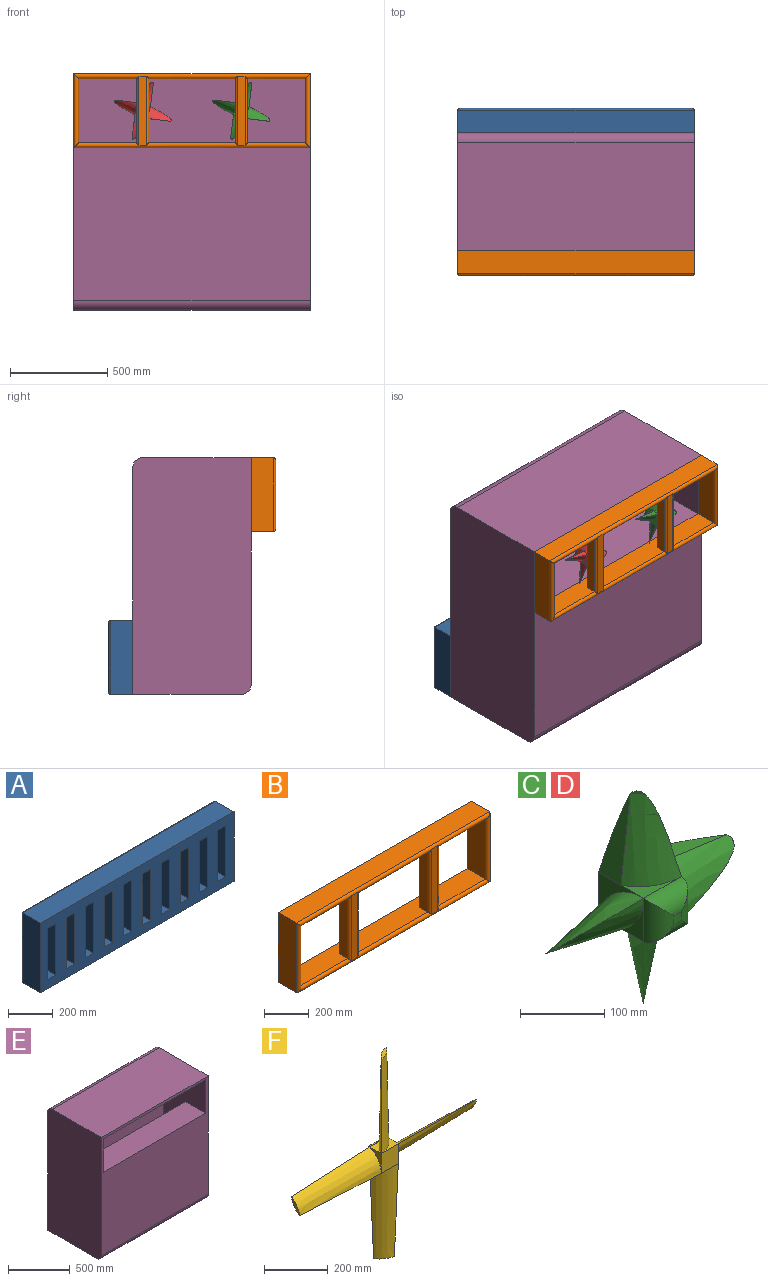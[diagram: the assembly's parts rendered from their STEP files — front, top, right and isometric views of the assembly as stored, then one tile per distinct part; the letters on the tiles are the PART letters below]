
ASSEMBLY  parts=6 mates=5
PART A: 90 faces, bbox 1219.2x127x381 mm
  f0: plane 1193.8x355.6mm, normal (0,1,0), area 192257.7mm2, adj f46,f47,f48,f49,f50,f51,f52,f53
  f1: plane 1219.2x381mm, normal (0,-1,0), area 322580mm2, adj f2,f3,f4,f5,f6,f7,f8,f9
  f2: plane 1219.2x114.3mm, normal (0,0,1), area 139354.6mm2, adj f1,f3,f5,f86
  f3: plane 381x114.3mm, normal (1,0,0), area 43548.3mm2, adj f1,f2,f4,f87
  f4: plane 1219.2x114.3mm, normal (0,0,-1), area 139354.6mm2, adj f1,f3,f5,f89
  f5: plane 381x114.3mm, normal (-1,0,0), area 43548.3mm2, adj f1,f2,f4,f88
  f6: plane 279.4x114.3mm, normal (1,0,0), area 31935.4mm2, adj f1,f7,f9,f84
  f7: plane 114.3x50.8mm, normal (0,0,-1), area 5806.4mm2, adj f1,f6,f8,f85
  f8: plane 279.4x114.3mm, normal (-1,0,0), area 31935.4mm2, adj f1,f7,f9,f83
  f9: plane 114.3x50.8mm, normal (0,0,1), area 5806.4mm2, adj f1,f6,f8,f82
  f10: plane 279.4x114.3mm, normal (1,0,0), area 31935.4mm2, adj f1,f11,f13,f78
  f11: plane 114.3x50.8mm, normal (0,0,-1), area 5806.4mm2, adj f1,f10,f12,f79
  f12: plane 279.4x114.3mm, normal (-1,0,0), area 31935.4mm2, adj f1,f11,f13,f81
  f13: plane 114.3x50.8mm, normal (0,0,1), area 5806.4mm2, adj f1,f10,f12,f80
  f14: plane 279.4x114.3mm, normal (1,0,0), area 31935.4mm2, adj f1,f15,f17,f76
  f15: plane 114.3x50.8mm, normal (0,0,-1), area 5806.4mm2, adj f1,f14,f16,f77
  f16: plane 279.4x114.3mm, normal (-1,0,0), area 31935.4mm2, adj f1,f15,f17,f75
  f17: plane 114.3x50.8mm, normal (0,0,1), area 5806.4mm2, adj f1,f14,f16,f74
  f18: plane 279.4x114.3mm, normal (1,0,0), area 31935.4mm2, adj f1,f19,f21,f72
  f19: plane 114.3x50.8mm, normal (0,0,-1), area 5806.4mm2, adj f1,f18,f20,f73
  f20: plane 279.4x114.3mm, normal (-1,0,0), area 31935.4mm2, adj f1,f19,f21,f71
  f21: plane 114.3x50.8mm, normal (0,0,1), area 5806.4mm2, adj f1,f18,f20,f70
  f22: plane 279.4x114.3mm, normal (1,0,0), area 31935.4mm2, adj f1,f23,f25,f68
  f23: plane 114.3x50.8mm, normal (0,0,-1), area 5806.4mm2, adj f1,f22,f24,f69
  f24: plane 279.4x114.3mm, normal (-1,0,0), area 31935.4mm2, adj f1,f23,f25,f67
  f25: plane 114.3x50.8mm, normal (0,0,1), area 5806.4mm2, adj f1,f22,f24,f66
  f26: plane 279.4x114.3mm, normal (1,0,0), area 31935.4mm2, adj f1,f27,f29,f64
  f27: plane 114.3x50.8mm, normal (0,0,-1), area 5806.4mm2, adj f1,f26,f28,f65
  f28: plane 279.4x114.3mm, normal (-1,0,0), area 31935.4mm2, adj f1,f27,f29,f63
  f29: plane 114.3x50.8mm, normal (0,0,1), area 5806.4mm2, adj f1,f26,f28,f62
  f30: plane 279.4x114.3mm, normal (1,0,0), area 31935.4mm2, adj f1,f31,f33,f60
  f31: plane 114.3x50.8mm, normal (0,0,-1), area 5806.4mm2, adj f1,f30,f32,f61
  f32: plane 279.4x114.3mm, normal (-1,0,0), area 31935.4mm2, adj f1,f31,f33,f59
  f33: plane 114.3x50.8mm, normal (0,0,1), area 5806.4mm2, adj f1,f30,f32,f58
  f34: plane 279.4x114.3mm, normal (1,0,0), area 31935.4mm2, adj f1,f35,f37,f56
  f35: plane 114.3x50.8mm, normal (0,0,-1), area 5806.4mm2, adj f1,f34,f36,f57
  f36: plane 279.4x114.3mm, normal (-1,0,0), area 31935.4mm2, adj f1,f35,f37,f55
  f37: plane 114.3x50.8mm, normal (0,0,1), area 5806.4mm2, adj f1,f34,f36,f54
  f38: plane 279.4x114.3mm, normal (1,0,0), area 31935.4mm2, adj f1,f39,f41,f52
  f39: plane 114.3x50.8mm, normal (0,0,-1), area 5806.4mm2, adj f1,f38,f40,f53
  f40: plane 279.4x114.3mm, normal (-1,0,0), area 31935.4mm2, adj f1,f39,f41,f51
  f41: plane 114.3x50.8mm, normal (0,0,1), area 5806.4mm2, adj f1,f38,f40,f50
  f42: plane 279.4x114.3mm, normal (1,0,0), area 31935.4mm2, adj f1,f43,f45,f48
  f43: plane 114.3x50.8mm, normal (0,0,-1), area 5806.4mm2, adj f1,f42,f44,f49
  f44: plane 279.4x114.3mm, normal (-1,0,0), area 31935.4mm2, adj f1,f43,f45,f47
  f45: plane 114.3x50.8mm, normal (0,0,1), area 5806.4mm2, adj f1,f42,f44,f46
  f46: cylinder r=12.7mm len=76.2mm, axis (1,0,0), area 1197.5mm2, adj f0,f45,f47,f48
  f47: cylinder r=12.7mm len=304.8mm, axis (0,0,1), area 5757.9mm2, adj f0,f44,f46,f49
  f48: cylinder r=12.7mm len=304.8mm, axis (0,0,-1), area 5757.9mm2, adj f0,f42,f46,f49
  f49: cylinder r=12.7mm len=76.2mm, axis (-1,0,0), area 1197.5mm2, adj f0,f43,f47,f48
  f50: cylinder r=12.7mm len=76.2mm, axis (1,0,0), area 1197.5mm2, adj f0,f41,f51,f52
  f51: cylinder r=12.7mm len=304.8mm, axis (0,0,1), area 5757.9mm2, adj f0,f40,f50,f53
  f52: cylinder r=12.7mm len=304.8mm, axis (0,0,-1), area 5757.9mm2, adj f0,f38,f50,f53
  f53: cylinder r=12.7mm len=76.2mm, axis (-1,0,0), area 1197.5mm2, adj f0,f39,f51,f52
  f54: cylinder r=12.7mm len=76.2mm, axis (1,0,0), area 1197.5mm2, adj f0,f37,f55,f56
  f55: cylinder r=12.7mm len=304.8mm, axis (0,0,1), area 5757.9mm2, adj f0,f36,f54,f57
  f56: cylinder r=12.7mm len=304.8mm, axis (0,0,-1), area 5757.9mm2, adj f0,f34,f54,f57
  f57: cylinder r=12.7mm len=76.2mm, axis (-1,0,0), area 1197.5mm2, adj f0,f35,f55,f56
  f58: cylinder r=12.7mm len=76.2mm, axis (1,0,0), area 1197.5mm2, adj f0,f33,f59,f60
  f59: cylinder r=12.7mm len=304.8mm, axis (0,0,1), area 5757.9mm2, adj f0,f32,f58,f61
  f60: cylinder r=12.7mm len=304.8mm, axis (0,0,-1), area 5757.9mm2, adj f0,f30,f58,f61
  f61: cylinder r=12.7mm len=76.2mm, axis (-1,0,0), area 1197.5mm2, adj f0,f31,f59,f60
  f62: cylinder r=12.7mm len=76.2mm, axis (1,0,0), area 1197.5mm2, adj f0,f29,f63,f64
  f63: cylinder r=12.7mm len=304.8mm, axis (0,0,1), area 5757.9mm2, adj f0,f28,f62,f65
  f64: cylinder r=12.7mm len=304.8mm, axis (0,0,-1), area 5757.9mm2, adj f0,f26,f62,f65
  f65: cylinder r=12.7mm len=76.2mm, axis (-1,0,0), area 1197.5mm2, adj f0,f27,f63,f64
  f66: cylinder r=12.7mm len=76.2mm, axis (1,0,0), area 1197.5mm2, adj f0,f25,f67,f68
  f67: cylinder r=12.7mm len=304.8mm, axis (0,0,1), area 5757.9mm2, adj f0,f24,f66,f69
  f68: cylinder r=12.7mm len=304.8mm, axis (0,0,-1), area 5757.9mm2, adj f0,f22,f66,f69
  f69: cylinder r=12.7mm len=76.2mm, axis (-1,0,0), area 1197.5mm2, adj f0,f23,f67,f68
  f70: cylinder r=12.7mm len=76.2mm, axis (1,0,0), area 1197.5mm2, adj f0,f21,f71,f72
  f71: cylinder r=12.7mm len=304.8mm, axis (0,0,1), area 5757.9mm2, adj f0,f20,f70,f73
  f72: cylinder r=12.7mm len=304.8mm, axis (0,0,-1), area 5757.9mm2, adj f0,f18,f70,f73
  f73: cylinder r=12.7mm len=76.2mm, axis (-1,0,0), area 1197.5mm2, adj f0,f19,f71,f72
  f74: cylinder r=12.7mm len=76.2mm, axis (1,0,0), area 1197.5mm2, adj f0,f17,f75,f76
  f75: cylinder r=12.7mm len=304.8mm, axis (0,0,1), area 5757.9mm2, adj f0,f16,f74,f77
  f76: cylinder r=12.7mm len=304.8mm, axis (0,0,-1), area 5757.9mm2, adj f0,f14,f74,f77
  f77: cylinder r=12.7mm len=76.2mm, axis (-1,0,0), area 1197.5mm2, adj f0,f15,f75,f76
  f78: cylinder r=12.7mm len=304.8mm, axis (0,0,-1), area 5757.9mm2, adj f0,f10,f79,f80
  f79: cylinder r=12.7mm len=76.2mm, axis (-1,0,0), area 1197.5mm2, adj f0,f11,f78,f81
  f80: cylinder r=12.7mm len=76.2mm, axis (1,0,0), area 1197.5mm2, adj f0,f13,f78,f81
  f81: cylinder r=12.7mm len=304.8mm, axis (0,0,1), area 5757.9mm2, adj f0,f12,f79,f80
  f82: cylinder r=12.7mm len=76.2mm, axis (1,0,0), area 1197.5mm2, adj f0,f9,f83,f84
  f83: cylinder r=12.7mm len=304.8mm, axis (0,0,1), area 5757.9mm2, adj f0,f8,f82,f85
  f84: cylinder r=12.7mm len=304.8mm, axis (0,0,-1), area 5757.9mm2, adj f0,f6,f82,f85
  f85: cylinder r=12.7mm len=76.2mm, axis (-1,0,0), area 1197.5mm2, adj f0,f7,f83,f84
  f86: cylinder r=12.7mm len=1219.2mm, axis (-1,0,0), area 24137.8mm2, adj f0,f2,f87,f88
  f87: cylinder r=12.7mm len=381mm, axis (0,0,1), area 7416.5mm2, adj f0,f3,f86,f89
  f88: cylinder r=12.7mm len=381mm, axis (0,0,-1), area 7416.5mm2, adj f0,f5,f86,f89
  f89: cylinder r=12.7mm len=1219.2mm, axis (1,0,0), area 24137.8mm2, adj f0,f4,f87,f88
PART B: 25 faces, bbox 1219.2x127x381 mm
  f0: plane 355.6x38.1mm, normal (0,-1,0), area 13548.4mm2, adj f17,f19,f20,f22
  f1: plane 355.6x38.1mm, normal (0,-1,0), area 13548.4mm2, adj f17,f18,f22,f24
  f2: plane 1219.2x381mm, normal (0,1,0), area 78709.5mm2, adj f3,f4,f5,f6,f7,f8,f9,f10
  f3: plane 381x114.3mm, normal (-1,0,0), area 43548.3mm2, adj f2,f4,f6,f21
  f4: plane 1219.2x114.3mm, normal (0,0,-1), area 139354.6mm2, adj f2,f3,f5,f17
  f5: plane 381x114.3mm, normal (1,0,0), area 43548.3mm2, adj f2,f4,f6,f23
  f6: plane 1219.2x114.3mm, normal (0,0,1), area 139354.6mm2, adj f2,f3,f5,f22
  f7: plane 1168.4x114.3mm, normal (0,0,-1), area 127096.5mm2, adj f2,f8,f10,f11,f12,f13,f14,f15
  f8: plane 330.2x114.3mm, normal (1,0,0), area 37741.9mm2, adj f2,f7,f9,f21
  f9: plane 1168.4x114.3mm, normal (0,0,1), area 127096.5mm2, adj f2,f8,f10,f11,f12,f13,f14,f15
  f10: plane 330.2x114.3mm, normal (-1,0,0), area 37741.9mm2, adj f2,f7,f9,f23
  f11: plane 330.2x50.8mm, normal (1,0,0), area 16774.2mm2, adj f7,f9,f13,f19
  f12: plane 330.2x50.8mm, normal (-1,0,0), area 16774.2mm2, adj f7,f9,f13,f20
  f13: plane 330.2x63.5mm, normal (0,1,0), area 20967.7mm2, adj f7,f9,f11,f12
  f14: plane 330.2x50.8mm, normal (1,0,0), area 16774.2mm2, adj f7,f9,f16,f24
  f15: plane 330.2x50.8mm, normal (-1,0,0), area 16774.2mm2, adj f7,f9,f16,f18
  f16: plane 330.2x63.5mm, normal (0,1,0), area 20967.7mm2, adj f7,f9,f14,f15
  f17: cylinder r=12.7mm len=1219.2mm, axis (-1,0,0), area 45465.2mm2, adj f0,f1,f4,f9,f18,f19,f20,f21
  f18: cylinder r=12.7mm len=355.6mm, axis (0,0,-1), area 6771.3mm2, adj f1,f15,f17,f22
  f19: cylinder r=12.7mm len=355.6mm, axis (0,0,1), area 6771.3mm2, adj f0,f11,f17,f22
  f20: cylinder r=12.7mm len=355.6mm, axis (0,0,-1), area 6771.3mm2, adj f0,f12,f17,f22
  f21: cylinder r=12.7mm len=381mm, axis (0,0,1), area 14187.8mm2, adj f3,f8,f17,f22
  f22: cylinder r=12.7mm len=1219.2mm, axis (1,0,0), area 45465.2mm2, adj f0,f1,f6,f7,f18,f19,f20,f21
  f23: cylinder r=12.7mm len=381mm, axis (0,0,-1), area 14187.8mm2, adj f5,f10,f17,f22
  f24: cylinder r=12.7mm len=355.6mm, axis (0,0,1), area 6771.3mm2, adj f1,f14,f17,f22
PART C: 26 faces, bbox 311.3x101.6x311.3 mm
  f0: plane 76.2x63.5mm, normal (0,0,1), area 1201.4mm2, adj f4,f8,f9,f21
  f1: plane 76.2x63.5mm, normal (-1,0,0), area 1201.4mm2, adj f5,f8,f17,f19
  f2: plane 76.2x63.5mm, normal (0,0,-1), area 1201.4mm2, adj f6,f8,f14,f18
  f3: plane 76.2x63.5mm, normal (1,0,0), area 1201.4mm2, adj f7,f8,f11,f15
  f4: plane 63.5x38.1mm, normal (1,0,0), area 695.7mm2, adj f0,f10,f24
  f5: plane 63.5x38.1mm, normal (0,0,1), area 695.7mm2, adj f1,f20,f22
  f6: plane 63.5x38.1mm, normal (-1,0,0), area 695.7mm2, adj f2,f16,f23
  f7: plane 63.5x38.1mm, normal (0,0,-1), area 695.7mm2, adj f3,f13,f25
  f8: plane 63.5x63.5mm, normal (0,1,0), area 4032.2mm2, adj f0,f1,f2,f3
  f9: plane 120.31x38.1mm, normal (0.17,0,0.98), area 2515mm2, adj f0,f10,f11
  f10: cone r=71.97mm half-angle=10deg, axis (-1,0,0), area 6254.7mm2, adj f4,f9,f11
  f11: cone r=77.47mm half-angle=10deg, axis (-1,0,0), area 8170.4mm2, adj f3,f9,f10
  f12: plane 12.7x12.7mm, normal (0,-1,0), area 161.3mm2, adj f22,f23,f24,f25
  f13: cone r=71.97mm half-angle=10deg, axis (0,0,1), area 6254.7mm2, adj f7,f14,f15
  f14: cone r=77.47mm half-angle=10deg, axis (0,0,1), area 8170.4mm2, adj f2,f13,f15
  f15: plane 120.31x38.1mm, normal (0.98,0,-0.17), area 2515mm2, adj f3,f13,f14
  f16: cone r=71.97mm half-angle=10deg, axis (1,0,0), area 6254.7mm2, adj f6,f17,f18
  f17: cone r=77.47mm half-angle=10deg, axis (1,0,0), area 8170.4mm2, adj f1,f16,f18
  f18: plane 120.31x38.1mm, normal (-0.17,0,-0.98), area 2515mm2, adj f2,f16,f17
  f19: plane 120.31x38.1mm, normal (-0.98,0,0.17), area 2515mm2, adj f1,f20,f21
  f20: cone r=71.97mm half-angle=10deg, axis (0,0,-1), area 6254.7mm2, adj f5,f19,f21
  f21: cone r=77.47mm half-angle=10deg, axis (0,0,-1), area 8170.4mm2, adj f0,f19,f20
  f22: cylinder r=25.4mm len=63.5mm, axis (1,0,0), area 1797mm2, adj f5,f12,f23,f24
  f23: cylinder r=25.4mm len=63.5mm, axis (0,0,1), area 1797mm2, adj f6,f12,f22,f25
  f24: cylinder r=25.4mm len=63.5mm, axis (0,0,-1), area 1797mm2, adj f4,f12,f22,f25
  f25: cylinder r=25.4mm len=63.5mm, axis (1,0,0), area 1797mm2, adj f7,f12,f23,f24
PART D: same geometry as C
PART E: 18 faces, bbox 1219.2x609.6x1219.2 mm
  f0: plane 1168.4x228.6mm, normal (0,0,1), area 267096.2mm2, adj f5,f11,f12,f15
  f1: plane 279.4x127mm, normal (1,0,0), area 35483.8mm2, adj f2,f4,f13,f14
  f2: plane 1125.22x127mm, normal (0,0,-1), area 142902.9mm2, adj f1,f3,f4,f13
  f3: plane 279.4x127mm, normal (-1,0,0), area 35483.8mm2, adj f2,f4,f13,f14
  f4: plane 1219.2x1168.4mm, normal (0,1,0), area 1110126.8mm2, adj f1,f2,f3,f6,f7,f9,f14,f17
  f5: plane 1219.2x1168.4mm, normal (0,-1,0), area 1038707.6mm2, adj f0,f6,f7,f8,f10,f11,f12,f16
  f6: plane 1219.2x609.6mm, normal (1,0,0), area 742116.7mm2, adj f4,f5,f8,f9,f16,f17
  f7: plane 1219.2x609.6mm, normal (-1,0,0), area 742116.7mm2, adj f4,f5,f8,f9,f16,f17
  f8: plane 1219.2x558.8mm, normal (0,0,1), area 681289mm2, adj f5,f6,f7,f17
  f9: plane 1219.2x558.8mm, normal (0,0,-1), area 681289mm2, adj f4,f6,f7,f16
  f10: plane 1168.4x482.6mm, normal (0,0,-1), area 563869.8mm2, adj f5,f11,f12,f13
  f11: plane 1143x482.6mm, normal (1,0,0), area 365805.7mm2, adj f0,f5,f10,f13,f14,f15
  f12: plane 1143x482.6mm, normal (-1,0,0), area 365805.7mm2, adj f0,f5,f10,f13,f14,f15
  f13: plane 1168.4x1143mm, normal (0,-1,0), area 1021094.7mm2, adj f1,f2,f3,f10,f11,f12,f14
  f14: plane 1168.4x381mm, normal (0,0,1), area 439676.5mm2, adj f1,f3,f4,f11,f12,f13,f15
  f15: plane 1168.4x812.8mm, normal (0,1,0), area 949675.5mm2, adj f0,f11,f12,f14
  f16: cylinder r=50.8mm len=1219.2mm, axis (1,0,0), area 97287.8mm2, adj f5,f6,f7,f9
  f17: cylinder r=50.8mm len=1219.2mm, axis (1,0,0), area 97287.8mm2, adj f4,f6,f7,f8
PART F: 43 faces, bbox 787.4x65.9x787.4 mm
  f0: plane 0.04x0mm, normal (-1,0,0), area 0mm2, adj f5,f6,f11
  f1: plane 50.7x0.04mm, normal (-1,0,0), area 2.2mm2, adj f5,f7,f10,f12
  f2: plane 50.8x0.04mm, normal (1,0,0), area 2.2mm2, adj f4,f5,f7,f14
  f3: cone r=82.55mm half-angle=1deg, axis (-1,0,0), area 29676.2mm2, adj f4,f6,f8,f13,f18
  f4: cone r=82.55mm half-angle=1deg, axis (-1,0,0), area 29676.2mm2, adj f2,f3,f8,f14,f18
  f5: plane 76.2x50.8mm, normal (0,0,-1), area 2147.5mm2, adj f0,f1,f2,f6,f7,f11,f12
  f6: plane 76.29x76.29mm, normal (0,1,0), area 19.5mm2, adj f0,f3,f5,f11,f13,f16,f18,f20
  f7: plane 76.29x76.29mm, normal (0,-1,0), area 5819.5mm2, adj f1,f2,f5,f10,f14,f15,f18,f21
  f8: plane 55.46x36.97mm, normal (1,0,0), area 687.6mm2, adj f3,f4
  f9: plane 50.8x50.8mm, normal (0,1,0), area 2574.1mm2, adj f31,f32,f33,f34,f35,f36,f37,f38
  f10: plane 50.8x0.04mm, normal (0,0,-1), area 2.2mm2, adj f1,f7,f12,f29
  f11: cone r=82.55mm half-angle=1deg, axis (0,0,1), area 29676.2mm2, adj f0,f5,f6,f12,f30
  f12: cone r=82.55mm half-angle=1deg, axis (0,0,1), area 29676.2mm2, adj f1,f5,f10,f11,f30
  f13: plane 0.04x0mm, normal (0,0,-1), area 0mm2, adj f3,f6,f18
  f14: plane 50.7x0.04mm, normal (0,0,-1), area 2.2mm2, adj f2,f4,f7,f18
  f15: plane 50.8x0.04mm, normal (0,0,1), area 2.2mm2, adj f7,f17,f18,f24
  f16: cone r=82.55mm half-angle=1deg, axis (0,0,-1), area 29676.2mm2, adj f6,f17,f19,f20,f25
  f17: cone r=82.55mm half-angle=1deg, axis (0,0,-1), area 29676.2mm2, adj f15,f16,f19,f24,f25
  f18: plane 76.2x50.8mm, normal (1,0,0), area 2147.5mm2, adj f3,f4,f6,f7,f13,f14,f15
  f19: plane 55.46x36.97mm, normal (0,0,1), area 687.6mm2, adj f16,f17
  f20: plane 0.04x0mm, normal (1,0,0), area 0mm2, adj f6,f16,f25
  f21: plane 50.8x0.04mm, normal (-1,0,0), area 2.2mm2, adj f7,f23,f25,f28
  f22: cone r=82.55mm half-angle=1deg, axis (1,0,0), area 29676.2mm2, adj f6,f23,f26,f27,f29
  f23: cone r=82.55mm half-angle=1deg, axis (1,0,0), area 29676.2mm2, adj f21,f22,f26,f28,f29
  f24: plane 50.7x0.04mm, normal (1,0,0), area 2.2mm2, adj f7,f15,f17,f25
  f25: plane 76.2x50.8mm, normal (0,0,1), area 2147.5mm2, adj f6,f7,f16,f17,f20,f21,f24
  f26: plane 55.46x36.97mm, normal (-1,0,0), area 687.6mm2, adj f22,f23
  f27: plane 0.04x0mm, normal (0,0,1), area 0mm2, adj f6,f22,f29
  f28: plane 50.7x0.04mm, normal (0,0,1), area 2.2mm2, adj f7,f21,f23,f29
  f29: plane 76.2x50.8mm, normal (-1,0,0), area 2147.5mm2, adj f6,f7,f10,f22,f23,f27,f28
  f30: plane 55.46x36.97mm, normal (0,0,-1), area 687.6mm2, adj f11,f12
  f31: cylinder r=12.7mm len=50.8mm, axis (0,0,-1), area 760.1mm2, adj f6,f9,f32,f33
  f32: cylinder r=12.7mm len=38.06mm, axis (-1,0,0), area 575.1mm2, adj f6,f9,f31,f34
  f33: cylinder r=12.7mm len=12.74mm, axis (-1,0,0), area 0.9mm2, adj f6,f9,f31,f35
  f34: cylinder r=12.7mm len=12.74mm, axis (0,0,1), area 0.9mm2, adj f6,f9,f32,f36
  f35: cylinder r=12.7mm len=38.06mm, axis (0,0,-1), area 575.1mm2, adj f6,f9,f33,f37
  f36: cylinder r=12.7mm len=50.8mm, axis (-1,0,0), area 760.1mm2, adj f6,f9,f34,f38
  f37: cylinder r=12.7mm len=50.8mm, axis (1,0,0), area 760.1mm2, adj f6,f9,f35,f39
  f38: cylinder r=12.7mm len=38.06mm, axis (0,0,1), area 575.1mm2, adj f6,f9,f36,f40
  f39: cylinder r=12.7mm len=12.74mm, axis (0,0,-1), area 0.9mm2, adj f6,f9,f37,f41
  f40: cylinder r=12.7mm len=12.74mm, axis (1,0,0), area 0.9mm2, adj f6,f9,f38,f42
  f41: cylinder r=12.7mm len=38.06mm, axis (-1,0,0), area 575.1mm2, adj f6,f9,f39,f42
  f42: cylinder r=12.7mm len=50.8mm, axis (0,0,1), area 760.1mm2, adj f6,f9,f40,f41
PLACE A t=(-629.68,-20.02,-170.52)mm
PLACE B t=(-629.68,-20.02,-170.52)mm
PLACE C rot(axis=(-0.15,0,-0.99),180deg) t=(-921.06,-820.12,-50.28)mm
PLACE D rot(axis=(-0.15,0,-0.99),180deg) t=(-1429.06,-820.12,-50.28)mm
PLACE E t=(-629.68,-20.02,-170.52)mm fixed
PLACE F rot(axis=(0,1,0),162.9deg) t=(-805.43,-20.02,857.67)mm
MATE revolute B.f16 <-> C.f8  axis (0,1,0) through (-375.68,-388.32,858.18)mm
MATE revolute D.f8 <-> B.f13  axis (0,-1,0) through (-883.68,-388.32,858.18)mm
MATE fastened E.f4 <-> A.f1  axis (0,1,0) through (-20.08,284.78,-170.52)mm
MATE revolute E.f15 <-> F.f7  axis (0,1,0) through (-629.68,-96.22,286.68)mm
MATE fastened B.f2 <-> E.f5  axis (0,1,0) through (-20.08,-324.82,1048.68)mm
